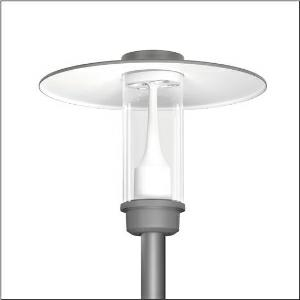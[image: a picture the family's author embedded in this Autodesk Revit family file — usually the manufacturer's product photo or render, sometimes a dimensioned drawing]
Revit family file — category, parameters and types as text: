
# Revit family: litepole_2_iq___p1_0a_5xa5425nf14h_2791
name_source: partatom
category: Lighting Fixtures
units: mm (PartAtom-declared; Revit-internal decimal feet)

## family parameters
Cut with Voids When Loaded = No
Host = Face
Light Source = No
Part Type = Normal
Room Calculation Point = No
Round Connector Dimension = Use Diameter
Shared = No

## types (1)
- --- (1 x LED, 1520 lm, 11.8 W, 2700K)
    Apparent Load = 12 VA
    CIE Flux Codes = 33 62 89 96 100
    Color Rendering = 70
    Color Temperature = 2700K
    Default Elevation = 1800 mm
    Description = Litepole 2 iQ, mast luminaire, Module 540 iQ-SR, primary light control with 3 zone facetted reflector, of plastic, silver coated, highly specular, structured, primary optical cover: cover, of PMMA, transparent, light distribution: P1.0a, light emission: direct distribution, primary light characteristic: strongly asymmetric, installation type: post-top, LED, High Power LED, rated luminous flux: 1.520lm, luminous efficacy: 129lm/W, light colour: 727, colour temperature: 2700K, control gear: iQ Street-Remote, control: pre-setting: logarithmic dimming characteristic, Street-Remote, Auto-Match, Temp-Guard, Lumen-Switch, Night-Set, Smart-Wire, Light-Fading, Desk-Remote (wireless, voltage-free reading and setting of iQ features in the workshop via application-optimized NFC function/RFID function), optimised constant luminous flux control (CLO 2.0), with terminal, 6-pole, max. 2.5mm², mains connection: 230..240V, AC, 50/60Hz, start of lifetime: 12W, end of service life: 12W, reduction: 6W, luminaire housing, upper part, of aluminium, coated, Siteco® metallic grey (DB 702S), diameter: 750mm, height: 590mm, spigot size: d x l = 76 x 70mm (post-top) | with reducer (optional accessory) 60 x 70mm, mounting height: 3..5m, post-top mast mounting element, of diecast aluminium, coated, Siteco® metallic grey (DB 702S), Module 540 iQ-SR, traffic white (RAL 9016), equipment: standard, protection rating (complete): IP65, insulation class (complete): insulation class II (safety insulation), certification: CE, ENEC, VDE, packaging unit: 1 piece

Light Distribution: P1.0a
    Height = 590 mm
    Lamp = 1 x LED
    Lamp Light Flux = 1520 lm
    Lamp Power = 11.8 W
    Lamp count = 1
    Length = 750 mm
    Luminous efficacy = 129 lm/W
    Manufacturer = Siteco
    ModVariant = No
    Model = 5XA5425NF14H
    Number of Poles = 1
    OnlyDefault = Yes
    Power Factor = 1
    Product Name = Litepole 2 iQ | P1.0a
    Product group = mast luminaire | pylon top
    ProductGroupID = 6100
    Protection Class = Protection class II
    Protection Degree = IP 65
    RLX_Detail_Level = 1
    RLX_Emergency_Light_Flux = 0 lm
    RLX_Emergency_Type = 0
    RLX_Emergency_Type_DB = No
    RlxData = <blob elided: 55189 chars, md5=56ab5ed0>
    Socket = socket
    Standby Power = 0 W
    System Light Flux = 1520 lm
    System Power = 12 W
    Type Comments = factory setting: luminous flux: 100 % | dim-lin: 254 | 472 mA
    Type Image = l_1006518.jpg
    URL = http://relux.com
    VarID = @adj_151893
    Voltage = 0 V
    Weight = 0.00 kg
    Width = 0 mm  [stored 0 ft]

note: [stored X ft] marks values corroborated as IEEE doubles in the binary element streams (Revit-internal decimal feet)

## geometry (parser evidence)
native form markers: Blend x4, Sweep x12
no freeform markers — native parametric forms only
